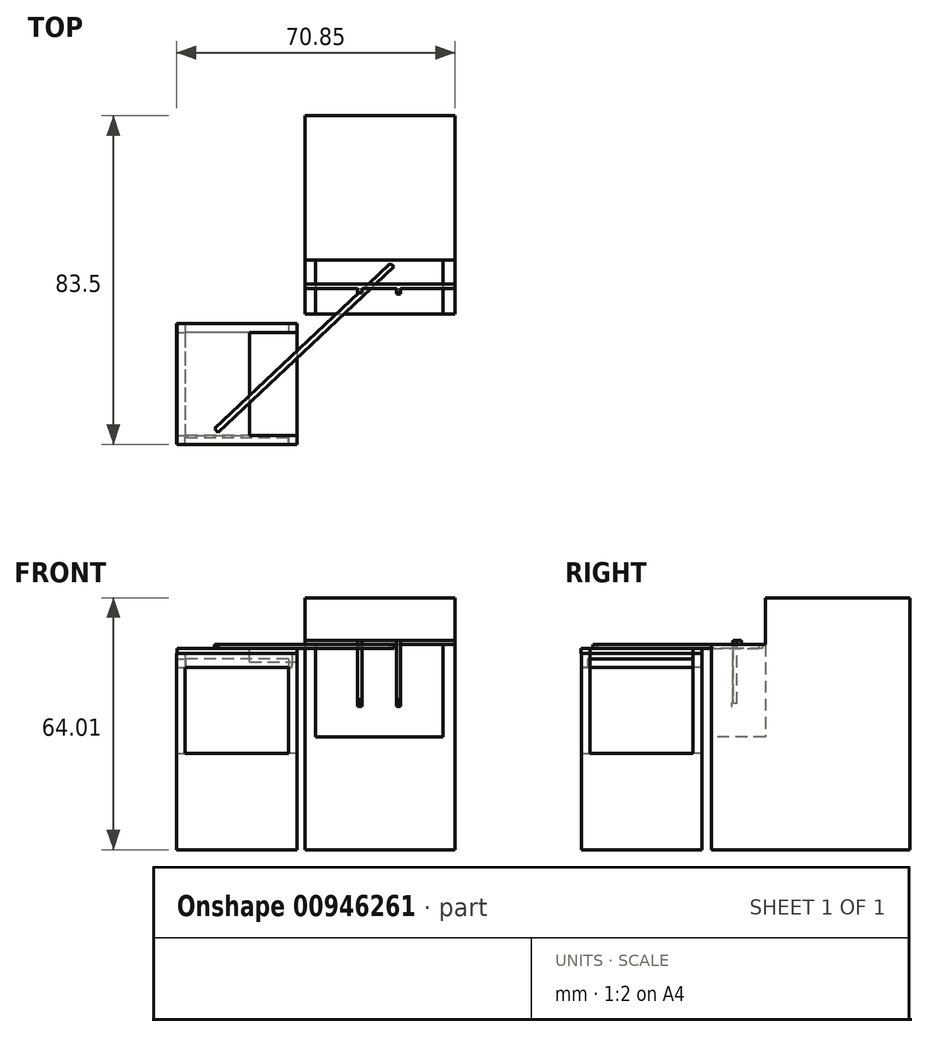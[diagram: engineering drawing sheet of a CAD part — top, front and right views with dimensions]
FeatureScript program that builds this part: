
annotation { "Feature Type Name" : "Feature", "Feature Type Description" : "" }
export const myFeature = defineFeature(function(context is Context, id is Id, definition is map)
    precondition{}
    {
        {
            var Q0;
            Q0=qCreatedBy(makeId("Top.planeOp"),FACE);
            var sketch = newSketch(context, id + "F0", { "sketchPlane" : qUnion([Q0])});
            skLineSegment(sketch, "E0.bottom", {"start": v(-69.44, -2.41) * mm, "end": v(-38.85, -2.41) * mm});
            skLineSegment(sketch, "E0.top", {"start": v(-69.44, -33) * mm, "end": v(-38.85, -33) * mm});
            skLineSegment(sketch, "E0.left", {"start": v(-69.44, -2.41) * mm, "end": v(-69.44, -33) * mm});
            skLineSegment(sketch, "E0.right", {"start": v(-38.85, -2.41) * mm, "end": v(-38.85, -33) * mm});
            skSolve(sketch);
        }
        {
            var Q0;
            Q0=makeQuery(id+"F0.imprint","IMPRINT",FACE,{"disambiguationData":[TD([[makeQuery(id+"F0.imprint","IMPRINT",EDGE,{"derivedFrom":sQuery(id+"F0.wireOp",EDGE,"E0.bottom")}),-1.0]])]});
            extrude(context, id + "F1", {"entities" : qUnion([Q0]), "depth" : 24.46 * mm, "offsetDistance" : 25.4 * mm});
        }
        {
            var Q0;
            Q0=qCreatedBy(makeId("Top.planeOp"),FACE);
            var sketch = newSketch(context, id + "F2", { "sketchPlane" : qUnion([Q0])});
            skLineSegment(sketch, "E1.bottom", {"start": v(-36.8, 0) * mm, "end": v(1.4, 0) * mm});
            skLineSegment(sketch, "E1.top", {"start": v(-36.8, 50.44) * mm, "end": v(1.4, 50.44) * mm});
            skLineSegment(sketch, "E1.left", {"start": v(-36.8, 0) * mm, "end": v(-36.8, 50.44) * mm});
            skLineSegment(sketch, "E1.right", {"start": v(1.4, 0) * mm, "end": v(1.4, 50.44) * mm});
            skSolve(sketch);
        }
        {
            var Q0;
            Q0=makeQuery(id+"F2.imprint","IMPRINT",FACE,{"disambiguationData":[TD([[makeQuery(id+"F2.imprint","IMPRINT",EDGE,{"derivedFrom":sQuery(id+"F2.wireOp",EDGE,"E1.bottom")}),1.0]])]});
            extrude(context, id + "F3", {"entities" : qUnion([Q0]), "depth" : 64 * mm, "offsetDistance" : 25.4 * mm});
        }
        {
            var Q0;
            Q0=makeQuery(id+"F3.opExtrude","SWEPT_FACE",FACE,{"disambiguationData":[OSD([sQuery(id+"F2.wireOp",EDGE,"E1.bottom")])]});
            var sketch = newSketch(context, id + "F4", { "sketchPlane" : qUnion([Q0])});
            skLineSegment(sketch, "E2.bottom", {"start": v(-34.03, 52.15) * mm, "end": v(-1.76, 52.15) * mm});
            skLineSegment(sketch, "E2.top", {"start": v(-34.03, 28.72) * mm, "end": v(-1.76, 28.72) * mm});
            skLineSegment(sketch, "E2.left", {"start": v(-34.03, 52.15) * mm, "end": v(-34.03, 28.72) * mm});
            skLineSegment(sketch, "E2.right", {"start": v(-1.76, 52.15) * mm, "end": v(-1.76, 28.72) * mm});
            skLineSegment(sketch, "E3", {"start": v(-36.8, 52.15) * mm, "end": v(-34.03, 52.15) * mm});
            skLineSegment(sketch, "E4", {"start": v(-36.8, 52.15) * mm, "end": v(-36.8, 64) * mm});
            skLineSegment(sketch, "E5", {"start": v(-36.8, 64) * mm, "end": v(1.4, 64) * mm});
            skLineSegment(sketch, "E6", {"start": v(1.4, 64) * mm, "end": v(1.4, 52.15) * mm});
            skLineSegment(sketch, "E7", {"start": v(1.4, 52.15) * mm, "end": v(-1.76, 52.15) * mm});
            skSolve(sketch);
        }
        {
            var Q0;
            Q0 = qSketchRegion(id + "F4", true);
            extrude(context, id + "F5", {"entities" : qUnion([Q0]), "operationType" : NewBodyOperationType.REMOVE, "oppositeDirection" : true, "depth" : 13.72 * mm, "offsetDistance" : 25.4 * mm});
        }
        {
            var Q0;
            Q0=makeQuery(id+"F1.opExtrude","CAP_FACE",FACE,{"disambiguationData":[OSD([sQuery(id+"F0.wireOp",EDGE,"E0.bottom"),sQuery(id+"F0.wireOp",EDGE,"E0.top"),sQuery(id+"F0.wireOp",EDGE,"E0.left"),sQuery(id+"F0.wireOp",EDGE,"E0.right")])],"isStart":false});
            var sketch = newSketch(context, id + "F6", { "sketchPlane" : qUnion([Q0])});
            skLineSegment(sketch, "E8.bottom", {"start": v(-69.44, -2.41) * mm, "end": v(-67.2, -2.41) * mm});
            skLineSegment(sketch, "E8.top", {"start": v(-69.44, -4.64) * mm, "end": v(-67.2, -4.64) * mm});
            skLineSegment(sketch, "E8.left", {"start": v(-69.44, -2.41) * mm, "end": v(-69.44, -4.64) * mm});
            skLineSegment(sketch, "E8.right", {"start": v(-67.2, -2.41) * mm, "end": v(-67.2, -4.64) * mm});
            skLineSegment(sketch, "E9.bottom", {"start": v(-38.85, -2.41) * mm, "end": v(-41, -2.41) * mm});
            skLineSegment(sketch, "E9.top", {"start": v(-38.85, -4.64) * mm, "end": v(-41, -4.64) * mm});
            skLineSegment(sketch, "E9.left", {"start": v(-38.85, -2.41) * mm, "end": v(-38.85, -4.64) * mm});
            skLineSegment(sketch, "E9.right", {"start": v(-41, -2.41) * mm, "end": v(-41, -4.64) * mm});
            skLineSegment(sketch, "E10.bottom", {"start": v(-38.85, -33) * mm, "end": v(-41, -33) * mm});
            skLineSegment(sketch, "E10.top", {"start": v(-38.85, -30.83) * mm, "end": v(-41, -30.83) * mm});
            skLineSegment(sketch, "E10.left", {"start": v(-38.85, -33) * mm, "end": v(-38.85, -30.83) * mm});
            skLineSegment(sketch, "E10.right", {"start": v(-41, -33) * mm, "end": v(-41, -30.83) * mm});
            skLineSegment(sketch, "E11.bottom", {"start": v(-69.44, -33) * mm, "end": v(-67.2, -33) * mm});
            skLineSegment(sketch, "E11.top", {"start": v(-69.44, -30.83) * mm, "end": v(-67.2, -30.83) * mm});
            skLineSegment(sketch, "E11.left", {"start": v(-69.44, -33) * mm, "end": v(-69.44, -30.83) * mm});
            skLineSegment(sketch, "E11.right", {"start": v(-67.2, -33) * mm, "end": v(-67.2, -30.83) * mm});
            skSolve(sketch);
        }
        {
            var Q0;
            Q0=makeQuery(id+"F6.imprint","IMPRINT",FACE,{"disambiguationData":[TD([[makeQuery(id+"F6.imprint","IMPRINT",EDGE,{"derivedFrom":sQuery(id+"F6.wireOp",EDGE,"E10.bottom")}),1.0]])]});
            var Q1;
            Q1=makeQuery(id+"F6.imprint","IMPRINT",FACE,{"disambiguationData":[TD([[makeQuery(id+"F6.imprint","IMPRINT",EDGE,{"derivedFrom":sQuery(id+"F6.wireOp",EDGE,"E9.bottom")}),-1.0]])]});
            var Q2;
            Q2=makeQuery(id+"F6.imprint","IMPRINT",FACE,{"disambiguationData":[TD([[makeQuery(id+"F6.imprint","IMPRINT",EDGE,{"derivedFrom":sQuery(id+"F6.wireOp",EDGE,"E8.bottom")}),-1.0]])]});
            var Q3;
            Q3=makeQuery(id+"F6.imprint","IMPRINT",FACE,{"disambiguationData":[TD([[makeQuery(id+"F6.imprint","IMPRINT",EDGE,{"derivedFrom":sQuery(id+"F6.wireOp",EDGE,"E11.bottom")}),1.0]])]});
            extrude(context, id + "F7", {"entities" : qUnion([Q0, Q1, Q2, Q3]), "operationType" : NewBodyOperationType.ADD, "depth" : 25.4 * mm, "offsetDistance" : 25.4 * mm});
        }
        {
            var Q0;
            Q0=makeQuery(id+"F7.opExtrude","CAP_EDGE",EDGE,{"disambiguationData":[OSD([sQuery(id+"F6.wireOp",EDGE,"E11.bottom")])],"isStart":false});
            cPoint(context, id + "F8", {"entities" : qUnion([Q0]), "parameter" : 0.5});
        }
        {
            var Q0;
            Q0 = qCreatedBy(id + "F8" ,VERTEX);
            var Q1;
            Q1=makeQuery(id+"F7.opExtrude","CAP_VERTEX",VERTEX,{"disambiguationData":[OSD([sQuery(id+"F6.wireOp",EDGE,"E8.top"),sQuery(id+"F6.wireOp",EDGE,"E8.right")])],"isStart":false});
            var Q2;
            Q2=makeQuery(id+"F7.opExtrude","CAP_VERTEX",VERTEX,{"disambiguationData":[OSD([sQuery(id+"F6.wireOp",EDGE,"E10.bottom"),sQuery(id+"F6.wireOp",EDGE,"E10.left")])],"isStart":false});
            cPlane(context, id + "F9", {"entities" : qUnion([Q0, Q1, Q2]), "cplaneType" : CPlaneType.THREE_POINT, "offset" : 25.4 * mm, "width" : 152.4 * mm, "height" : 152.4 * mm});
        }
        {
            var Q0;
            Q0=qCreatedBy(id+"F9.planeOp",FACE);
            var sketch = newSketch(context, id + "F10", { "sketchPlane" : qUnion([Q0])});
            skLineSegment(sketch, "E12.bottom", {"start": v(-69.32, -2.35) * mm, "end": v(-38.76, -2.35) * mm});
            skLineSegment(sketch, "E12.top", {"start": v(-69.32, -33.06) * mm, "end": v(-38.76, -33.06) * mm});
            skLineSegment(sketch, "E12.left", {"start": v(-69.32, -2.35) * mm, "end": v(-69.32, -33.06) * mm});
            skLineSegment(sketch, "E12.right", {"start": v(-38.76, -2.35) * mm, "end": v(-38.76, -33.06) * mm});
            skSolve(sketch);
        }
        {
            var Q0;
            Q0=makeQuery(id+"F10.imprint","IMPRINT",FACE,{"disambiguationData":[TD([[makeQuery(id+"F10.imprint","IMPRINT",EDGE,{"derivedFrom":sQuery(id+"F10.wireOp",EDGE,"E12.bottom")}),-1.0]])]});
            extrude(context, id + "F11", {"entities" : qUnion([Q0]), "operationType" : NewBodyOperationType.ADD, "depth" : 1.27 * mm, "offsetDistance" : 25.4 * mm});
        }
        {
            var Q0;
            Q0=makeQuery(id+"F5.boolean.opBoolean","COPY",VERTEX,{"derivedFrom":makeQuery(id+"F5.opExtrude","CAP_VERTEX",VERTEX,{"disambiguationData":[OSD([sQuery(id+"F4.wireOp",EDGE,"E2.bottom"),sQuery(id+"F4.wireOp",EDGE,"E2.left"),sQuery(id+"F4.wireOp",EDGE,"E3")])],"isStart":true})});
            var Q1;
            Q1=makeQuery(id+"F5.boolean.opBoolean","COPY",VERTEX,{"derivedFrom":makeQuery(id+"F5.opExtrude","CAP_VERTEX",VERTEX,{"disambiguationData":[OSD([sQuery(id+"F2.wireOp",EDGE,"E1.bottom"),sQuery(id+"F2.wireOp",EDGE,"E1.left"),sQuery(id+"F4.wireOp",EDGE,"E3"),sQuery(id+"F4.wireOp",EDGE,"E4")])],"isStart":false})});
            var Q2;
            Q2=makeQuery(id+"F5.boolean.opBoolean","COPY",VERTEX,{"derivedFrom":makeQuery(id+"F5.opExtrude","CAP_VERTEX",VERTEX,{"disambiguationData":[OSD([sQuery(id+"F2.wireOp",EDGE,"E1.bottom"),sQuery(id+"F2.wireOp",EDGE,"E1.right"),sQuery(id+"F4.wireOp",EDGE,"E6"),sQuery(id+"F4.wireOp",EDGE,"E7")])],"isStart":true})});
            cPlane(context, id + "F12", {"entities" : qUnion([Q0, Q1, Q2]), "cplaneType" : CPlaneType.THREE_POINT, "offset" : 25.4 * mm, "width" : 152.4 * mm, "height" : 152.4 * mm});
        }
        {
            var Q0;
            Q0=qCreatedBy(id+"F12.planeOp",FACE);
            var sketch = newSketch(context, id + "F13", { "sketchPlane" : qUnion([Q0])});
            skLineSegment(sketch, "E13.bottom", {"start": v(-36.75, 7.7) * mm, "end": v(1.4, 7.7) * mm});
            skLineSegment(sketch, "E13.top", {"start": v(-36.75, 6.54) * mm, "end": v(1.4, 6.54) * mm});
            skLineSegment(sketch, "E13.left", {"start": v(-36.75, 7.7) * mm, "end": v(-36.75, 6.54) * mm});
            skLineSegment(sketch, "E13.right", {"start": v(1.4, 7.7) * mm, "end": v(1.4, 6.54) * mm});
            skSolve(sketch);
        }
        {
            var Q0;
            Q0=makeQuery(id+"F13.imprint","IMPRINT",FACE,{"disambiguationData":[TD([[makeQuery(id+"F13.imprint","IMPRINT",EDGE,{"derivedFrom":sQuery(id+"F13.wireOp",EDGE,"E13.bottom")}),-1.0]])]});
            extrude(context, id + "F14", {"entities" : qUnion([Q0]), "operationType" : NewBodyOperationType.ADD, "depth" : 1.02 * mm, "offsetDistance" : 25.4 * mm});
        }
        {
            var Q0;
            Q0=makeQuery(id+"F7.opExtrude","SWEPT_FACE",FACE,{"disambiguationData":[OSD([sQuery(id+"F6.wireOp",EDGE,"E9.top")])]});
            var sketch = newSketch(context, id + "F15", { "sketchPlane" : qUnion([Q0])});
            skLineSegment(sketch, "E14.bottom", {"start": v(-69.45, 48.54) * mm, "end": v(-67.15, 48.54) * mm});
            skLineSegment(sketch, "E14.top", {"start": v(-69.45, 46.32) * mm, "end": v(-67.15, 46.32) * mm});
            skLineSegment(sketch, "E14.left", {"start": v(-69.45, 48.54) * mm, "end": v(-69.45, 46.32) * mm});
            skLineSegment(sketch, "E14.right", {"start": v(-67.15, 48.54) * mm, "end": v(-67.15, 46.32) * mm});
            skLineSegment(sketch, "E15.bottom", {"start": v(-41, 49.86) * mm, "end": v(-38.85, 49.86) * mm});
            skLineSegment(sketch, "E15.top", {"start": v(-41, 47.67) * mm, "end": v(-38.85, 47.67) * mm});
            skLineSegment(sketch, "E15.left", {"start": v(-41, 49.86) * mm, "end": v(-41, 47.67) * mm});
            skLineSegment(sketch, "E15.right", {"start": v(-38.85, 49.86) * mm, "end": v(-38.85, 47.67) * mm});
            skSolve(sketch);
        }
        {
            var Q0;
            Q0=makeQuery(id+"F15.imprint","IMPRINT",FACE,{"disambiguationData":[TD([[makeQuery(id+"F15.imprint","IMPRINT",EDGE,{"derivedFrom":sQuery(id+"F15.wireOp",EDGE,"E14.bottom")}),-1.0]])]});
            var Q1;
            Q1=makeQuery(id+"F15.imprint","IMPRINT",FACE,{"disambiguationData":[TD([[makeQuery(id+"F15.imprint","IMPRINT",EDGE,{"derivedFrom":sQuery(id+"F15.wireOp",EDGE,"E15.bottom")}),1.0]])]});
            extrude(context, id + "F16", {"entities" : qUnion([Q0, Q1]), "operationType" : NewBodyOperationType.ADD, "depth" : 26.8 * mm, "offsetDistance" : 25.4 * mm});
        }
        {
            var Q0;
            Q0=makeQuery(id+"F7.opExtrude","SWEPT_FACE",FACE,{"disambiguationData":[OSD([sQuery(id+"F6.wireOp",EDGE,"E11.right")])]});
            var sketch = newSketch(context, id + "F17", { "sketchPlane" : qUnion([Q0])});
            skLineSegment(sketch, "E16.bottom", {"start": v(-33, 49.86) * mm, "end": v(-30.83, 49.86) * mm});
            skLineSegment(sketch, "E16.top", {"start": v(-33, 46.32) * mm, "end": v(-30.83, 46.32) * mm});
            skLineSegment(sketch, "E16.left", {"start": v(-33, 49.86) * mm, "end": v(-33, 46.32) * mm});
            skLineSegment(sketch, "E16.right", {"start": v(-30.83, 49.86) * mm, "end": v(-30.83, 46.32) * mm});
            skLineSegment(sketch, "E17.bottom", {"start": v(-4.67, 46.32) * mm, "end": v(-2.37, 46.32) * mm});
            skLineSegment(sketch, "E17.top", {"start": v(-4.67, 49.86) * mm, "end": v(-2.37, 49.86) * mm});
            skLineSegment(sketch, "E17.left", {"start": v(-4.67, 46.32) * mm, "end": v(-4.67, 49.86) * mm});
            skLineSegment(sketch, "E17.right", {"start": v(-2.37, 46.32) * mm, "end": v(-2.37, 49.86) * mm});
            skSolve(sketch);
        }
        {
            var Q0;
            Q0=makeQuery(id+"F17.imprint","IMPRINT",FACE,{"disambiguationData":[TD([[makeQuery(id+"F17.imprint","IMPRINT",EDGE,{"derivedFrom":sQuery(id+"F17.wireOp",EDGE,"E17.bottom")}),1.0]])]});
            var Q1;
            {var subQ0=sQuery(id+"F17.wireOp",EDGE,"E16.left");Q1=makeQuery(id+"F17.imprint","IMPRINT",FACE,{"disambiguationData":[TD([[makeQuery(id+"F17.imprint","IMPRINT",EDGE,{"derivedFrom":subQ0}),1.0]])]});}
            extrude(context, id + "F18", {"entities" : qUnion([Q0, Q1]), "operationType" : NewBodyOperationType.ADD, "depth" : 27.13 * mm, "offsetDistance" : 25.4 * mm});
        }
        {
            var Q0;
            Q0=makeQuery(id+"F16.boolean.opBoolean","MERGE",FACE,{"derivedFrom":[makeQuery(id+"F7.boolean.opBoolean","MERGE",FACE,{"derivedFrom":[makeQuery(id+"F1.opExtrude","SWEPT_FACE",FACE,{"disambiguationData":[OSD([sQuery(id+"F0.wireOp",EDGE,"E0.right")])]}),makeQuery(id+"F7.opExtrude","SWEPT_FACE",FACE,{"disambiguationData":[OSD([sQuery(id+"F6.wireOp",EDGE,"E9.left")])]}),makeQuery(id+"F7.opExtrude","SWEPT_FACE",FACE,{"disambiguationData":[OSD([sQuery(id+"F6.wireOp",EDGE,"E10.left")])]})]}),makeQuery(id+"F16.opExtrude","SWEPT_FACE",FACE,{"disambiguationData":[OSD([sQuery(id+"F15.wireOp",EDGE,"E15.right")])]})]});
            var sketch = newSketch(context, id + "F19", { "sketchPlane" : qUnion([Q0])});
            skLineSegment(sketch, "E18.bottom", {"start": v(-30.83, 47.67) * mm, "end": v(-4.65, 47.67) * mm});
            skLineSegment(sketch, "E18.top", {"start": v(-30.83, 51.15) * mm, "end": v(-4.65, 51.15) * mm});
            skLineSegment(sketch, "E18.left", {"start": v(-30.83, 47.67) * mm, "end": v(-30.83, 51.15) * mm});
            skLineSegment(sketch, "E18.right", {"start": v(-4.65, 47.67) * mm, "end": v(-4.65, 51.15) * mm});
            skSolve(sketch);
        }
        {
            var Q0;
            {var subQ0=sQuery(id+"F19.wireOp",EDGE,"E18.top");Q0=makeQuery(id+"F19.imprint","IMPRINT",FACE,{"disambiguationData":[TD([[makeQuery(id+"F19.imprint","IMPRINT",EDGE,{"derivedFrom":subQ0}),-1.0]])]});}
            var Q1;
            {var subQ0=sQuery(id+"F19.wireOp",EDGE,"E18.bottom");Q1=makeQuery(id+"F19.imprint","IMPRINT",FACE,{"disambiguationData":[TD([[makeQuery(id+"F19.imprint","IMPRINT",EDGE,{"derivedFrom":subQ0}),1.0]])]});}
            extrude(context, id + "F20", {"entities" : qUnion([Q0, Q1]), "operationType" : NewBodyOperationType.REMOVE, "oppositeDirection" : true, "depth" : 12 * mm, "offsetDistance" : 25.4 * mm, "hasSecondDirection" : true, "secondDirectionOppositeDirection" : false, "secondDirectionDepth" : 25.4 * mm});
        }
        {
            var Q0;
            Q0=makeQuery(id+"F11.opExtrude","CAP_FACE",FACE,{"disambiguationData":[OSD([sQuery(id+"F10.wireOp",EDGE,"E12.bottom"),sQuery(id+"F10.wireOp",EDGE,"E12.top"),sQuery(id+"F10.wireOp",EDGE,"E12.left"),sQuery(id+"F10.wireOp",EDGE,"E12.right")])],"isStart":false});
            cPlane(context, id + "F21", {"entities" : qUnion([Q0]), "cplaneType" : CPlaneType.OFFSET, "offset" : 0 * mm, "width" : 152.4 * mm, "height" : 152.4 * mm});
        }
        {
            var Q0;
            Q0=qCreatedBy(id+"F21.planeOp",FACE);
            var sketch = newSketch(context, id + "F22", { "sketchPlane" : qUnion([Q0])});
            skLineSegment(sketch, "E19", {"start": v(-15.12, 12.94) * mm, "end": v(-59.76, -29.08) * mm});
            skLineSegment(sketch, "E20", {"start": v(-59.76, -29.08) * mm, "end": v(-58.88, -30.02) * mm});
            skLineSegment(sketch, "E21", {"start": v(-58.88, -30.02) * mm, "end": v(-14.14, 12.09) * mm});
            skLineSegment(sketch, "E22", {"start": v(-15.12, 12.94) * mm, "end": v(-14.14, 12.09) * mm});
            skSolve(sketch);
        }
        {
            var Q0;
            Q0=makeQuery(id+"F22.imprint","IMPRINT",FACE,{"disambiguationData":[TD([[makeQuery(id+"F22.imprint","IMPRINT",EDGE,{"derivedFrom":sQuery(id+"F22.wireOp",EDGE,"E19")}),1.0]])]});
            extrude(context, id + "F23", {"entities" : qUnion([Q0]), "depth" : 1.1 * mm, "offsetDistance" : 25.4 * mm});
        }
        {
            var Q0;
            Q0=makeQuery(id+"F14.opExtrude","CAP_FACE",FACE,{"disambiguationData":[OSD([sQuery(id+"F13.wireOp",EDGE,"E13.bottom"),sQuery(id+"F13.wireOp",EDGE,"E13.top"),sQuery(id+"F13.wireOp",EDGE,"E13.left"),sQuery(id+"F13.wireOp",EDGE,"E13.right")])],"isStart":false});
            var sketch = newSketch(context, id + "F24", { "sketchPlane" : qUnion([Q0])});
            skLineSegment(sketch, "E23.bottom", {"start": v(-23.37, 6.54) * mm, "end": v(-22.3, 6.54) * mm});
            skLineSegment(sketch, "E23.top", {"start": v(-23.37, 5.49) * mm, "end": v(-22.3, 5.49) * mm});
            skLineSegment(sketch, "E23.left", {"start": v(-23.37, 6.54) * mm, "end": v(-23.37, 5.49) * mm});
            skLineSegment(sketch, "E23.right", {"start": v(-22.3, 6.54) * mm, "end": v(-22.3, 5.49) * mm});
            skLineSegment(sketch, "E24.bottom", {"start": v(-13.52, 6.54) * mm, "end": v(-12.46, 6.54) * mm});
            skLineSegment(sketch, "E24.top", {"start": v(-13.52, 5.47) * mm, "end": v(-12.46, 5.47) * mm});
            skLineSegment(sketch, "E24.left", {"start": v(-13.52, 6.54) * mm, "end": v(-13.52, 5.47) * mm});
            skLineSegment(sketch, "E24.right", {"start": v(-12.46, 6.54) * mm, "end": v(-12.46, 5.47) * mm});
            skSolve(sketch);
        }
        {
            var Q0;
            Q0=makeQuery(id+"F24.imprint","IMPRINT",FACE,{"disambiguationData":[TD([[makeQuery(id+"F24.imprint","IMPRINT",EDGE,{"derivedFrom":sQuery(id+"F24.wireOp",EDGE,"E23.bottom")}),-1.0]])]});
            var Q1;
            Q1=makeQuery(id+"F24.imprint","IMPRINT",FACE,{"disambiguationData":[TD([[makeQuery(id+"F24.imprint","IMPRINT",EDGE,{"derivedFrom":sQuery(id+"F24.wireOp",EDGE,"E24.bottom")}),-1.0]])]});
            extrude(context, id + "F25", {"entities" : qUnion([Q0, Q1]), "operationType" : NewBodyOperationType.ADD, "oppositeDirection" : true, "depth" : 16 * mm, "offsetDistance" : 25.4 * mm});
        }
        {
            var Q0;
            Q0=makeQuery(id+"F25.opExtrude","SWEPT_FACE",FACE,{"disambiguationData":[OSD([sQuery(id+"F24.wireOp",EDGE,"E23.left")])]});
            var sketch = newSketch(context, id + "F26", { "sketchPlane" : qUnion([Q0])});
            skLineSegment(sketch, "E25", {"start": v(-5.49, 38.25) * mm, "end": v(-5.49, 37.49) * mm});
            skLineSegment(sketch, "E26", {"start": v(-5.49, 37.49) * mm, "end": v(-5.26, 37.26) * mm});
            skLineSegment(sketch, "E27", {"start": v(-5.26, 37.26) * mm, "end": v(-5.26, 36.44) * mm});
            skLineSegment(sketch, "E28", {"start": v(-5.26, 36.44) * mm, "end": v(-5.13, 36.44) * mm});
            skLineSegment(sketch, "E29", {"start": v(-5.13, 36.44) * mm, "end": v(-5.13, 37.26) * mm});
            skLineSegment(sketch, "E30", {"start": v(-5.13, 37.26) * mm, "end": v(-5.43, 37.57) * mm});
            skLineSegment(sketch, "E31", {"start": v(-5.43, 37.57) * mm, "end": v(-5.43, 38.26) * mm});
            skLineSegment(sketch, "E32", {"start": v(-5.43, 38.26) * mm, "end": v(-5.49, 38.25) * mm});
            skSolve(sketch);
        }
        {
            var Q0;
            Q0=makeQuery(id+"F26.imprint","IMPRINT",FACE,{"disambiguationData":[TD([[makeQuery(id+"F26.imprint","IMPRINT",EDGE,{"derivedFrom":sQuery(id+"F26.wireOp",EDGE,"E25")}),-1.0]])]});
            extrude(context, id + "F27", {"entities" : qUnion([Q0]), "operationType" : NewBodyOperationType.ADD, "oppositeDirection" : true, "depth" : 10.9 * mm, "offsetDistance" : 25.4 * mm});
        }
        {
            var Q0;
            Q0=makeQuery(id+"F27.opExtrude","SWEPT_FACE",FACE,{"disambiguationData":[OSD([sQuery(id+"F26.wireOp",EDGE,"E29")])]});
            var sketch = newSketch(context, id + "F28", { "sketchPlane" : qUnion([Q0])});
            skLineSegment(sketch, "E33.bottom", {"start": v(-22.3, 38.24) * mm, "end": v(-13.54, 38.24) * mm});
            skLineSegment(sketch, "E33.top", {"start": v(-22.3, 36.44) * mm, "end": v(-13.54, 36.44) * mm});
            skLineSegment(sketch, "E33.left", {"start": v(-22.3, 38.24) * mm, "end": v(-22.3, 36.44) * mm});
            skLineSegment(sketch, "E33.right", {"start": v(-13.54, 38.24) * mm, "end": v(-13.54, 36.44) * mm});
            skSolve(sketch);
        }
        {
            var Q0;
            {var subQ0=sQuery(id+"F28.wireOp",EDGE,"E33.top");Q0=makeQuery(id+"F28.imprint","IMPRINT",FACE,{"disambiguationData":[TD([[makeQuery(id+"F28.imprint","IMPRINT",EDGE,{"derivedFrom":subQ0}),-1.0]])]});}
            extrude(context, id + "F29", {"entities" : qUnion([Q0]), "operationType" : NewBodyOperationType.REMOVE, "oppositeDirection" : true, "depth" : 0.58 * mm, "offsetDistance" : 25.4 * mm});
        }
        {
            var Q0;
            Q0=makeQuery(id+"F5.boolean.opBoolean","COPY",FACE,{"derivedFrom":makeQuery(id+"F5.opExtrude","CAP_FACE",FACE,{"disambiguationData":[OSD([sQuery(id+"F4.wireOp",EDGE,"E2.top"),sQuery(id+"F4.wireOp",EDGE,"E2.left"),sQuery(id+"F4.wireOp",EDGE,"E2.right"),sQuery(id+"F4.wireOp",EDGE,"E3"),sQuery(id+"F4.wireOp",EDGE,"E4"),sQuery(id+"F4.wireOp",EDGE,"E5"),sQuery(id+"F4.wireOp",EDGE,"E6"),sQuery(id+"F4.wireOp",EDGE,"E7")])],"isStart":false})});
            var sketch = newSketch(context, id + "F30", { "sketchPlane" : qUnion([Q0])});
            skLineSegment(sketch, "E34.bottom", {"start": v(-22.3, 38.4) * mm, "end": v(-13.54, 38.4) * mm});
            skLineSegment(sketch, "E34.top", {"start": v(-22.3, 36) * mm, "end": v(-13.54, 36) * mm});
            skLineSegment(sketch, "E34.left", {"start": v(-22.3, 38.4) * mm, "end": v(-22.3, 36) * mm});
            skLineSegment(sketch, "E34.right", {"start": v(-13.54, 38.4) * mm, "end": v(-13.54, 36) * mm});
            skSolve(sketch);
        }
        {
            var Q0;
            Q0=makeQuery(id+"F30.imprint","IMPRINT",FACE,{"disambiguationData":[TD([[makeQuery(id+"F30.imprint","IMPRINT",EDGE,{"derivedFrom":sQuery(id+"F30.wireOp",EDGE,"E34.bottom")}),-1.0]])]});
            extrude(context, id + "F31", {"entities" : qUnion([Q0]), "operationType" : NewBodyOperationType.REMOVE, "depth" : 25.4 * mm, "offsetDistance" : 25.4 * mm});
        }
    });
